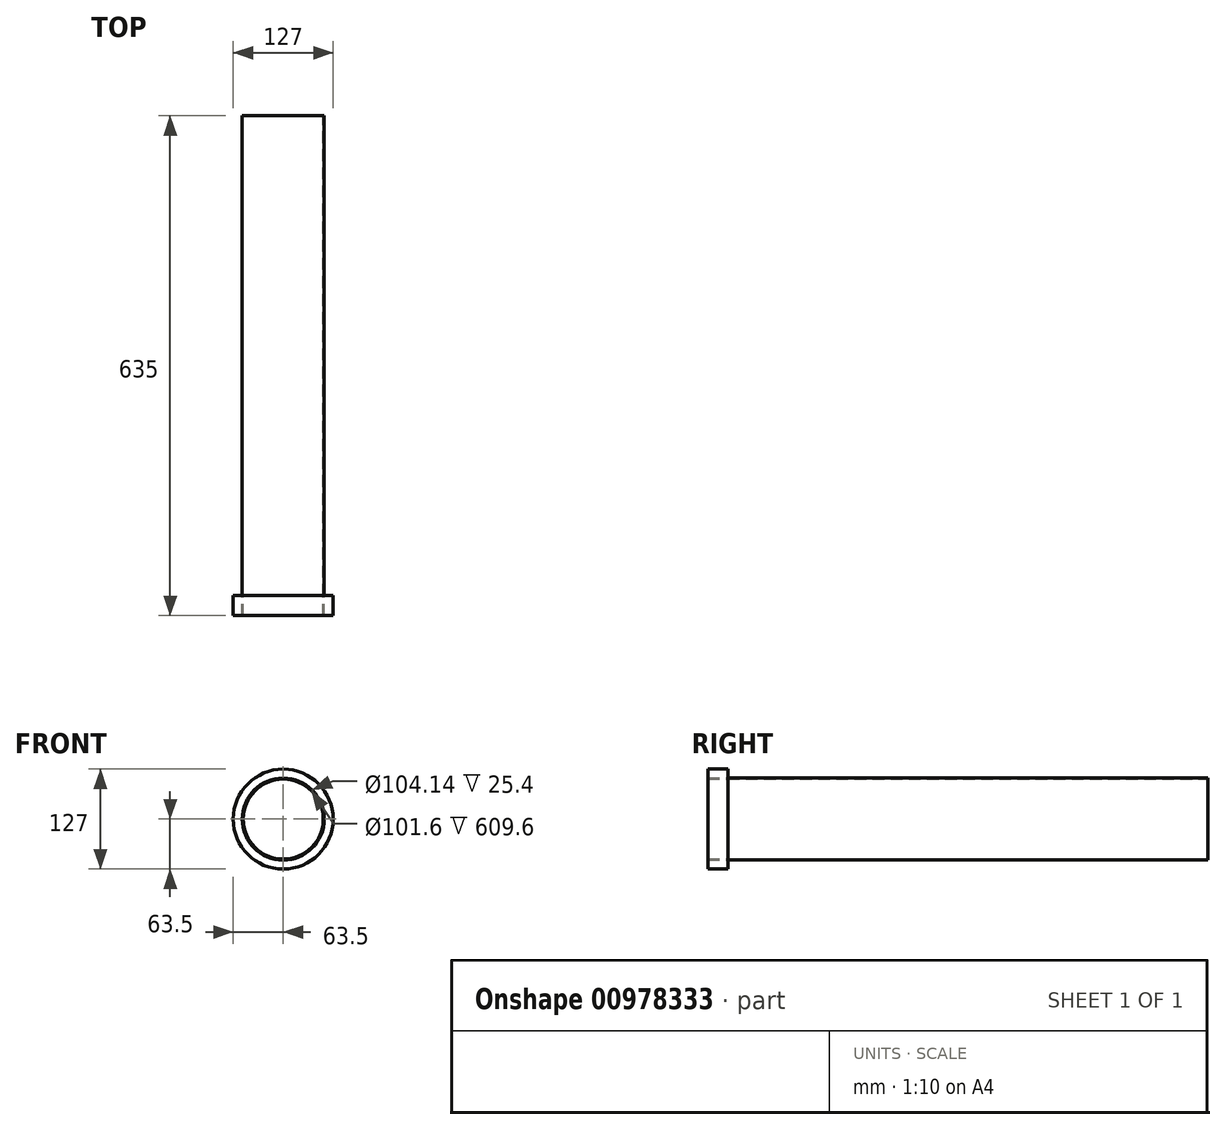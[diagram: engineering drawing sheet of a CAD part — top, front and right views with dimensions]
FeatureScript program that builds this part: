
annotation { "Feature Type Name" : "Feature", "Feature Type Description" : "" }
export const myFeature = defineFeature(function(context is Context, id is Id, definition is map)
    precondition{}
    {
        {
            var Q0;
            Q0=qCreatedBy(makeId("Front.planeOp"),FACE);
            var sketch = newSketch(context, id + "F0", { "sketchPlane" : qUnion([Q0])});
            skLineSegment(sketch, "E0", {"start": v(0, 0) * mm, "end": v(-76.2, 0) * mm});
            skLineSegment(sketch, "E1", {"start": v(0, 0) * mm, "end": v(50.38, 57.17) * mm});
            skCircle(sketch, "E2", {"center": v(0, 0) * mm, "radius": 50.8 * mm});
            skCircle(sketch, "E3", {"center": v(0, 0) * mm, "radius": 52.07 * mm});
            skSolve(sketch);
        }
        {
            var Q0;
            {var subQ0=sQuery(id+"F0.wireOp",EDGE,"E3");var subQ1=sQuery(id+"F0.wireOp",EDGE,"E0");var subQ2=makeQuery(id+"F0.imprint","INTERSECT",VERTEX,{"derivedFrom":[subQ1,subQ0]});Q0=makeQuery(id+"F0.imprint","IMPRINT",FACE,{"disambiguationData":[TD([[makeQuery(id+"F0.imprint","IMPRINT",EDGE,{"disambiguationData":[TD([[subQ2,1.0]])],"derivedFrom":subQ1}),1.0]])]});}
            var Q1;
            {var subQ0=sQuery(id+"F0.wireOp",EDGE,"E3");var subQ1=sQuery(id+"F0.wireOp",EDGE,"E0");var subQ2=makeQuery(id+"F0.imprint","INTERSECT",VERTEX,{"derivedFrom":[subQ1,subQ0]});Q1=makeQuery(id+"F0.imprint","IMPRINT",FACE,{"disambiguationData":[TD([[makeQuery(id+"F0.imprint","IMPRINT",EDGE,{"disambiguationData":[TD([[subQ2,1.0]])],"derivedFrom":subQ1}),-1.0]])]});}
            extrude(context, id + "F1", {"entities" : qUnion([Q0, Q1]), "endBound" : BoundingType.SYMMETRIC, "depth" : 609.6 * mm, "offsetDistance" : 25.4 * mm});
        }
        {
            var Q0;
            Q0=makeQuery(id+"F1.opExtrude","CAP_FACE",FACE,{"disambiguationData":[OSD([sQuery(id+"F0.wireOp",EDGE,"E2"),sQuery(id+"F0.wireOp",EDGE,"E3")])],"isStart":false});
            var sketch = newSketch(context, id + "F2", { "sketchPlane" : qUnion([Q0])});
            skCircle(sketch, "E4", {"center": v(0, 0) * mm, "radius": 63.5 * mm});
            skSolve(sketch);
        }
        {
            var Q0;
            Q0=makeQuery(id+"F2.imprint","IMPRINT",FACE,{"disambiguationData":[TD([[makeQuery(id+"F2.imprint","IMPRINT",EDGE,{"derivedFrom":sQuery(id+"F2.wireOp",EDGE,"E4")}),1.0]])]});
            var Q1;
            Q1=makeQuery(id+"F2.imprint","IMPRINT",FACE,{"disambiguationData":[TD([[makeQuery(id+"F2.imprint","IMPRINT",EDGE,{"derivedFrom":makeQuery(id+"F1.opExtrude","CAP_EDGE",EDGE,{"disambiguationData":[OSD([sQuery(id+"F0.wireOp",EDGE,"E2")])],"isStart":false})}),1.0]])]});
            extrude(context, id + "F3", {"entities" : qUnion([Q0, Q1]), "operationType" : NewBodyOperationType.ADD, "depth" : 25.4 * mm, "offsetDistance" : 25.4 * mm});
        }
    });
